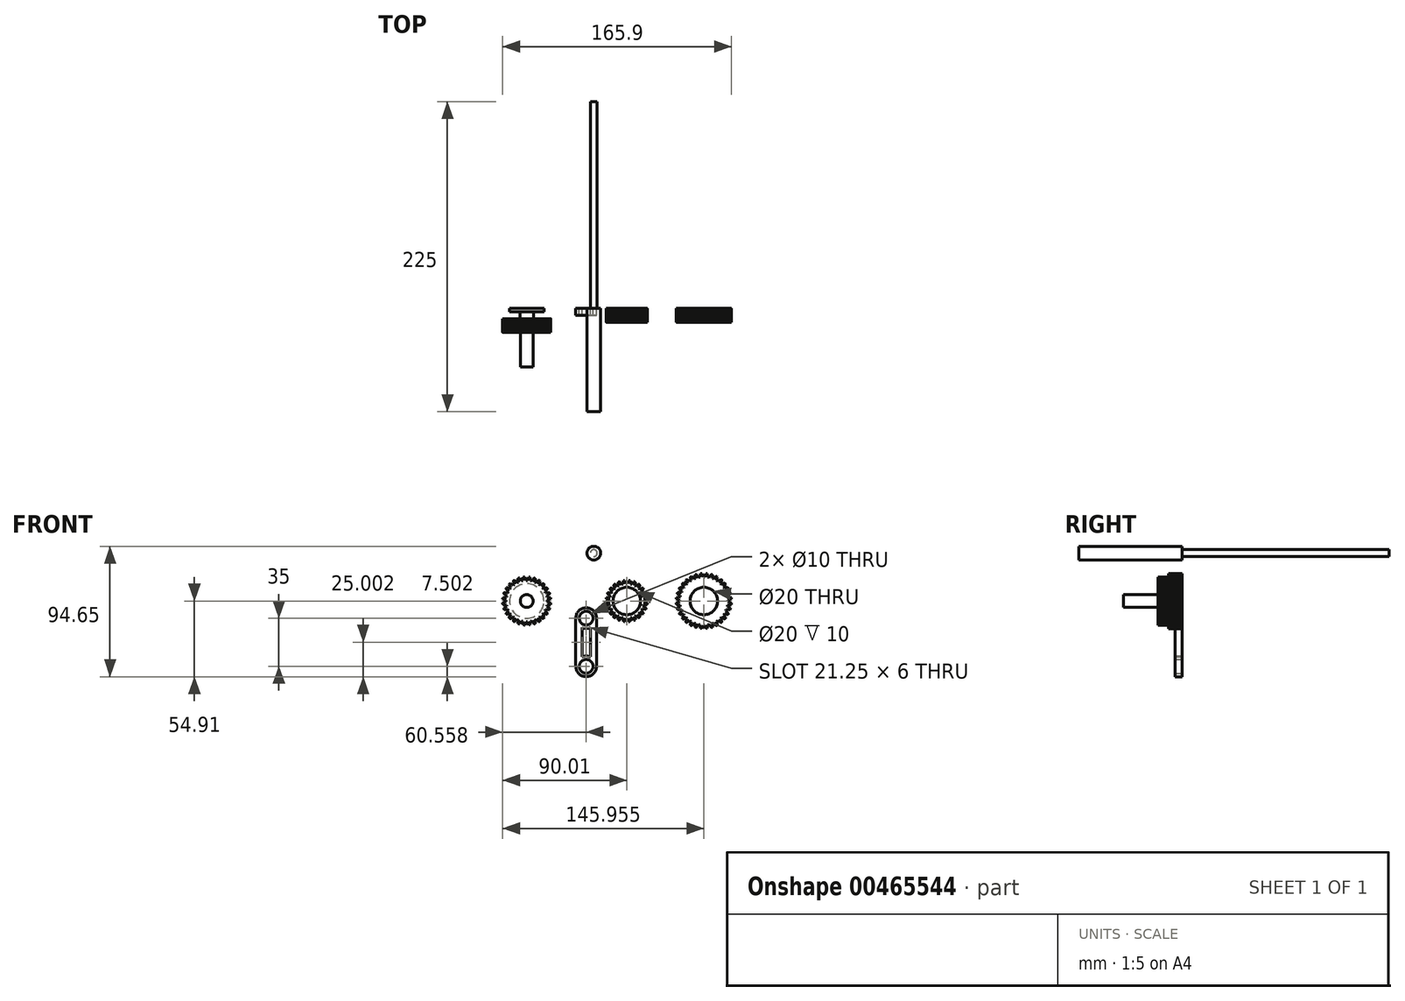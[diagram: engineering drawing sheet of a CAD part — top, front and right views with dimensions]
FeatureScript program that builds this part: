
annotation { "Feature Type Name" : "Feature", "Feature Type Description" : "" }
export const myFeature = defineFeature(function(context is Context, id is Id, definition is map)
    precondition{}
    {
        {
            var Q0;
            Q0=qCreatedBy(makeId("Front.planeOp"),FACE);
            var sketch = newSketch(context, id + "F0", { "sketchPlane" : qUnion([Q0])});
            skCircle(sketch, "E0", {"center": v(0, 0) * mm, "radius": 15 * mm});
            skCircle(sketch, "E1", {"center": v(0, 0) * mm, "radius": 10 * mm});
            skSolve(sketch);
        }
        {
            var Q0;
            Q0=makeQuery(id+"F0.imprint","IMPRINT",FACE,{"disambiguationData":[TD([[makeQuery(id+"F0.imprint","IMPRINT",EDGE,{"derivedFrom":sQuery(id+"F0.wireOp",EDGE,"E0")}),1.0]])]});
            extrude(context, id + "F1", {"entities" : qUnion([Q0]), "depth" : 10 * mm});
        }
        {
            var Q0;
            Q0=makeQuery(id+"F1.opExtrude","CAP_FACE",FACE,{"disambiguationData":[OSD([sQuery(id+"F0.wireOp",EDGE,"E0"),sQuery(id+"F0.wireOp",EDGE,"E1")])],"isStart":false});
            var sketch = newSketch(context, id + "F2", { "sketchPlane" : qUnion([Q0])});
            skLineSegment(sketch, "E2", {"start": v(0, 0) * mm, "end": v(0, 15) * mm, "construction": true});
            skLineSegment(sketch, "E3", {"start": v(0, 12.45) * mm, "end": v(0, 15) * mm, "construction": true});
            skLineSegment(sketch, "E4", {"start": v(0, 12.45) * mm, "end": v(-0.5, 12.45) * mm});
            skLineSegment(sketch, "E5", {"start": v(0, 12.45) * mm, "end": v(0.5, 12.45) * mm});
            skLineSegment(sketch, "E6", {"start": v(-0.5, 12.45) * mm, "end": v(-1.4, 14.93) * mm});
            skLineSegment(sketch, "E7", {"start": v(0.5, 12.45) * mm, "end": v(1.4, 14.93) * mm});
            skSolve(sketch);
        }
        {
            var Q0;
            Q0=makeQuery(id+"F2.imprint","IMPRINT",FACE,{"disambiguationData":[TD([[makeQuery(id+"F2.imprint","IMPRINT",EDGE,{"derivedFrom":sQuery(id+"F2.wireOp",EDGE,"E4")}),-1.0]])]});
            extrude(context, id + "F3", {"entities" : qUnion([Q0]), "operationType" : NewBodyOperationType.REMOVE, "oppositeDirection" : true, "depth" : 25 * mm});
        }
        {
            var Q0;
            Q0=makeQuery(id+"F3.boolean.opBoolean","COPY",FACE,{"derivedFrom":makeQuery(id+"F3.opExtrude","SWEPT_FACE",FACE,{"disambiguationData":[OSD([sQuery(id+"F2.wireOp",EDGE,"E6")])]})});
            var Q1;
            Q1=makeQuery(id+"F3.boolean.opBoolean","COPY",FACE,{"derivedFrom":makeQuery(id+"F3.opExtrude","SWEPT_FACE",FACE,{"disambiguationData":[OSD([sQuery(id+"F2.wireOp",EDGE,"E4"),sQuery(id+"F2.wireOp",EDGE,"E5")])]})});
            var Q2;
            Q2=makeQuery(id+"F3.boolean.opBoolean","COPY",FACE,{"derivedFrom":makeQuery(id+"F3.opExtrude","SWEPT_FACE",FACE,{"disambiguationData":[OSD([sQuery(id+"F2.wireOp",EDGE,"E7")])]})});
            var Q3;
            Q3=makeQuery(id+"F1.opExtrude","SWEPT_FACE",FACE,{"disambiguationData":[OSD([sQuery(id+"F0.wireOp",EDGE,"E0")])]});
            circularPattern(context, id + "F4", {"patternType" : PatternType.FACE, "faces" : qUnion([Q0, Q1, Q2]), "axis" : qUnion([Q3]), "angle" : 360 * degree, "instanceCount" : 24, "equalSpace" : true});
        }
        {
            var Q0;
            Q0=qCreatedBy(makeId("Front.planeOp"),FACE);
            var sketch = newSketch(context, id + "F5", { "sketchPlane" : qUnion([Q0])});
            skCircle(sketch, "E8", {"center": v(-72.57, 0) * mm, "radius": 12.5 * mm});
            skSolve(sketch);
        }
        {
            var Q0;
            Q0=makeQuery(id+"F5.imprint","IMPRINT",FACE,{"disambiguationData":[TD([[makeQuery(id+"F5.imprint","IMPRINT",EDGE,{"derivedFrom":sQuery(id+"F5.wireOp",EDGE,"E8")}),1.0]])]});
            extrude(context, id + "F6", {"entities" : qUnion([Q0]), "depth" : 2.5 * mm});
        }
        {
            var Q0;
            Q0=makeQuery(id+"F6.opExtrude","CAP_FACE",FACE,{"disambiguationData":[OSD([sQuery(id+"F5.wireOp",EDGE,"E8")])],"isStart":false});
            var sketch = newSketch(context, id + "F7", { "sketchPlane" : qUnion([Q0])});
            skLineSegment(sketch, "E9", {"start": v(-72.57, 0) * mm, "end": v(-72.57, 12.5) * mm, "construction": true});
            skLineSegment(sketch, "E10", {"start": v(-72.57, 0) * mm, "end": v(-72.57, -12.5) * mm, "construction": true});
            skCircle(sketch, "E11", {"center": v(-72.57, 0) * mm, "radius": 5 * mm});
            skSolve(sketch);
        }
        {
            var Q0;
            Q0=makeQuery(id+"F7.imprint","IMPRINT",FACE,{"disambiguationData":[TD([[makeQuery(id+"F7.imprint","IMPRINT",EDGE,{"derivedFrom":sQuery(id+"F7.wireOp",EDGE,"E11")}),1.0]])]});
            extrude(context, id + "F8", {"entities" : qUnion([Q0]), "depth" : 5 * mm});
        }
        {
            var Q0;
            Q0=makeQuery(id+"F8.opExtrude","CAP_FACE",FACE,{"disambiguationData":[OSD([sQuery(id+"F7.wireOp",EDGE,"E11")])],"isStart":false});
            var sketch = newSketch(context, id + "F9", { "sketchPlane" : qUnion([Q0])});
            skCircle(sketch, "E12", {"center": v(-72.57, 0) * mm, "radius": 17.5 * mm});
            skSolve(sketch);
        }
        {
            var Q0;
            Q0=makeQuery(id+"F9.imprint","IMPRINT",FACE,{"disambiguationData":[TD([[makeQuery(id+"F9.imprint","IMPRINT",EDGE,{"derivedFrom":sQuery(id+"F9.wireOp",EDGE,"E12")}),1.0]])]});
            var Q1;
            Q1=makeQuery(id+"F9.imprint","IMPRINT",FACE,{"disambiguationData":[TD([[makeQuery(id+"F9.imprint","IMPRINT",EDGE,{"derivedFrom":makeQuery(id+"F8.opExtrude","CAP_EDGE",EDGE,{"disambiguationData":[OSD([sQuery(id+"F7.wireOp",EDGE,"E11")])],"isStart":false})}),1.0]])]});
            extrude(context, id + "F10", {"entities" : qUnion([Q0, Q1]), "operationType" : NewBodyOperationType.ADD, "depth" : 10 * mm});
        }
        {
            var Q0;
            Q0=makeQuery(id+"F10.opExtrude","CAP_FACE",FACE,{"disambiguationData":[OSD([sQuery(id+"F9.wireOp",EDGE,"E12")])],"isStart":false});
            var sketch = newSketch(context, id + "F11", { "sketchPlane" : qUnion([Q0])});
            skLineSegment(sketch, "E13", {"start": v(-72.57, 0) * mm, "end": v(-72.57, 17.5) * mm, "construction": true});
            skLineSegment(sketch, "E14", {"start": v(-72.57, 17.5) * mm, "end": v(-72.57, 14.95) * mm, "construction": true});
            skLineSegment(sketch, "E15", {"start": v(-72.57, 14.95) * mm, "end": v(-72.07, 14.95) * mm});
            skLineSegment(sketch, "E16", {"start": v(-72.57, 14.95) * mm, "end": v(-73.07, 14.95) * mm});
            skLineSegment(sketch, "E17", {"start": v(-73.07, 14.95) * mm, "end": v(-73.98, 17.44) * mm});
            skLineSegment(sketch, "E18", {"start": v(-72.07, 14.95) * mm, "end": v(-71.16, 17.44) * mm});
            skSolve(sketch);
        }
        {
            var Q0;
            Q0=makeQuery(id+"F11.imprint","IMPRINT",FACE,{"disambiguationData":[TD([[makeQuery(id+"F11.imprint","IMPRINT",EDGE,{"derivedFrom":sQuery(id+"F11.wireOp",EDGE,"E15")}),1.0]])]});
            extrude(context, id + "F12", {"entities" : qUnion([Q0]), "operationType" : NewBodyOperationType.REMOVE, "oppositeDirection" : true, "depth" : 25 * mm});
        }
        {
            var Q0;
            Q0=makeQuery(id+"F12.boolean.opBoolean","COPY",FACE,{"derivedFrom":makeQuery(id+"F12.opExtrude","SWEPT_FACE",FACE,{"disambiguationData":[OSD([sQuery(id+"F11.wireOp",EDGE,"E17")])]})});
            var Q1;
            Q1=makeQuery(id+"F12.boolean.opBoolean","COPY",FACE,{"derivedFrom":makeQuery(id+"F12.opExtrude","SWEPT_FACE",FACE,{"disambiguationData":[OSD([sQuery(id+"F11.wireOp",EDGE,"E15"),sQuery(id+"F11.wireOp",EDGE,"E16")])]})});
            var Q2;
            Q2=makeQuery(id+"F12.boolean.opBoolean","COPY",FACE,{"derivedFrom":makeQuery(id+"F12.opExtrude","SWEPT_FACE",FACE,{"disambiguationData":[OSD([sQuery(id+"F11.wireOp",EDGE,"E18")])]})});
            var Q3;
            Q3=makeQuery(id+"F10.opExtrude","SWEPT_FACE",FACE,{"disambiguationData":[OSD([sQuery(id+"F9.wireOp",EDGE,"E12")])]});
            circularPattern(context, id + "F13", {"patternType" : PatternType.FACE, "faces" : qUnion([Q0, Q1, Q2]), "axis" : qUnion([Q3]), "angle" : 360 * degree, "instanceCount" : 28, "equalSpace" : true});
        }
        {
            var Q0;
            Q0=makeQuery(id+"F10.opExtrude","CAP_FACE",FACE,{"disambiguationData":[OSD([sQuery(id+"F9.wireOp",EDGE,"E12")])],"isStart":false});
            var sketch = newSketch(context, id + "F14", { "sketchPlane" : qUnion([Q0])});
            skCircle(sketch, "E19", {"center": v(-72.57, 0) * mm, "radius": 4.64 * mm});
            skSolve(sketch);
        }
        {
            var Q0;
            Q0=makeQuery(id+"F14.imprint","IMPRINT",FACE,{"disambiguationData":[TD([[makeQuery(id+"F14.imprint","IMPRINT",EDGE,{"derivedFrom":sQuery(id+"F14.wireOp",EDGE,"E19")}),1.0]])]});
            extrude(context, id + "F15", {"entities" : qUnion([Q0]), "operationType" : NewBodyOperationType.ADD, "depth" : 25 * mm});
        }
        {
            var Q0;
            Q0=qCreatedBy(makeId("Front.planeOp"),FACE);
            var sketch = newSketch(context, id + "F16", { "sketchPlane" : qUnion([Q0])});
            skCircle(sketch, "E20", {"center": v(55.94, 0) * mm, "radius": 10 * mm});
            skCircle(sketch, "E21", {"center": v(55.94, 0) * mm, "radius": 20 * mm});
            skSolve(sketch);
        }
        {
            var Q0;
            Q0=makeQuery(id+"F16.imprint","IMPRINT",FACE,{"disambiguationData":[TD([[makeQuery(id+"F16.imprint","IMPRINT",EDGE,{"derivedFrom":sQuery(id+"F16.wireOp",EDGE,"E20")}),-1.0]])]});
            extrude(context, id + "F17", {"entities" : qUnion([Q0]), "depth" : 10 * mm});
        }
        {
            var Q0;
            Q0=makeQuery(id+"F17.opExtrude","CAP_FACE",FACE,{"disambiguationData":[OSD([sQuery(id+"F16.wireOp",EDGE,"E20"),sQuery(id+"F16.wireOp",EDGE,"E21")])],"isStart":false});
            var sketch = newSketch(context, id + "F18", { "sketchPlane" : qUnion([Q0])});
            skLineSegment(sketch, "E22", {"start": v(55.94, 0) * mm, "end": v(55.94, 20) * mm, "construction": true});
            skLineSegment(sketch, "E23", {"start": v(55.94, 20) * mm, "end": v(55.94, 17.45) * mm, "construction": true});
            skLineSegment(sketch, "E24", {"start": v(55.94, 17.45) * mm, "end": v(55.44, 17.45) * mm});
            skLineSegment(sketch, "E25", {"start": v(55.94, 17.45) * mm, "end": v(56.44, 17.45) * mm});
            skLineSegment(sketch, "E26", {"start": v(55.44, 17.45) * mm, "end": v(54.53, 19.95) * mm});
            skLineSegment(sketch, "E27", {"start": v(56.44, 17.45) * mm, "end": v(57.35, 19.95) * mm});
            skSolve(sketch);
        }
        {
            var Q0;
            Q0=makeQuery(id+"F18.imprint","IMPRINT",FACE,{"disambiguationData":[TD([[makeQuery(id+"F18.imprint","IMPRINT",EDGE,{"derivedFrom":sQuery(id+"F18.wireOp",EDGE,"E24")}),-1.0]])]});
            extrude(context, id + "F19", {"entities" : qUnion([Q0]), "operationType" : NewBodyOperationType.REMOVE, "oppositeDirection" : true, "depth" : 25 * mm});
        }
        {
            var Q0;
            Q0=makeQuery(id+"F19.boolean.opBoolean","COPY",FACE,{"derivedFrom":makeQuery(id+"F19.opExtrude","SWEPT_FACE",FACE,{"disambiguationData":[OSD([sQuery(id+"F18.wireOp",EDGE,"E26")])]})});
            var Q1;
            Q1=makeQuery(id+"F19.boolean.opBoolean","COPY",FACE,{"derivedFrom":makeQuery(id+"F19.opExtrude","SWEPT_FACE",FACE,{"disambiguationData":[OSD([sQuery(id+"F18.wireOp",EDGE,"E24"),sQuery(id+"F18.wireOp",EDGE,"E25")])]})});
            var Q2;
            Q2=makeQuery(id+"F19.boolean.opBoolean","COPY",FACE,{"derivedFrom":makeQuery(id+"F19.opExtrude","SWEPT_FACE",FACE,{"disambiguationData":[OSD([sQuery(id+"F18.wireOp",EDGE,"E27")])]})});
            var Q3;
            Q3=makeQuery(id+"F17.opExtrude","SWEPT_FACE",FACE,{"disambiguationData":[OSD([sQuery(id+"F16.wireOp",EDGE,"E21")])]});
            circularPattern(context, id + "F20", {"patternType" : PatternType.FACE, "faces" : qUnion([Q0, Q1, Q2]), "axis" : qUnion([Q3]), "angle" : 360 * degree, "instanceCount" : 32, "equalSpace" : true});
        }
        {
            var Q0;
            Q0=qCreatedBy(makeId("Front.planeOp"),FACE);
            var sketch = newSketch(context, id + "F21", { "sketchPlane" : qUnion([Q0])});
            skCircle(sketch, "E28", {"center": v(-23.91, 34.74) * mm, "radius": 5 * mm});
            skSolve(sketch);
        }
        {
            var Q0;
            Q0=makeQuery(id+"F21.imprint","IMPRINT",FACE,{"disambiguationData":[TD([[makeQuery(id+"F21.imprint","IMPRINT",EDGE,{"derivedFrom":sQuery(id+"F21.wireOp",EDGE,"E28")}),1.0]])]});
            extrude(context, id + "F22", {"entities" : qUnion([Q0]), "depth" : 75 * mm});
        }
        {
            var Q0;
            Q0=makeQuery(id+"F22.opExtrude","CAP_FACE",FACE,{"disambiguationData":[OSD([sQuery(id+"F21.wireOp",EDGE,"E28")])],"isStart":true});
            var sketch = newSketch(context, id + "F23", { "sketchPlane" : qUnion([Q0])});
            skCircle(sketch, "E29", {"center": v(23.91, 34.74) * mm, "radius": 2.5 * mm});
            skSolve(sketch);
        }
        {
            var Q0;
            Q0=makeQuery(id+"F23.imprint","IMPRINT",FACE,{"disambiguationData":[TD([[makeQuery(id+"F23.imprint","IMPRINT",EDGE,{"derivedFrom":sQuery(id+"F23.wireOp",EDGE,"E29")}),1.0]])]});
            extrude(context, id + "F24", {"entities" : qUnion([Q0]), "operationType" : NewBodyOperationType.ADD, "depth" : 150 * mm});
        }
        {
            var Q0;
            Q0=qCreatedBy(makeId("Front.planeOp"),FACE);
            var sketch = newSketch(context, id + "F25", { "sketchPlane" : qUnion([Q0])});
            skCircle(sketch, "E30", {"center": v(-29.45, -12.4) * mm, "radius": 5 * mm});
            skLineSegment(sketch, "E31", {"start": v(-29.45, -12.4) * mm, "end": v(-29.45, -47.4) * mm, "construction": true});
            skCircle(sketch, "E32", {"center": v(-29.45, -47.4) * mm, "radius": 5 * mm});
            skCircle(sketch, "E33", {"center": v(-29.45, -12.4) * mm, "radius": 7.5 * mm});
            skCircle(sketch, "E34", {"center": v(-29.45, -47.4) * mm, "radius": 7.5 * mm});
            skLineSegment(sketch, "E35", {"start": v(-36.95, -12.4) * mm, "end": v(-36.95, -47.4) * mm});
            skLineSegment(sketch, "E36", {"start": v(-21.95, -47.4) * mm, "end": v(-21.95, -12.4) * mm});
            skPoint(sketch, "E37", {"position": v(-29.45, -39.9) * mm});
            skPoint(sketch, "E38", {"position": v(-29.45, -19.9) * mm});
            skLineSegment(sketch, "E39", {"start": v(-32.45, -39.9) * mm, "end": v(-32.45, -19.9) * mm});
            skLineSegment(sketch, "E40", {"start": v(-26.45, -19.9) * mm, "end": v(-26.45, -40.53) * mm});
            skLineSegment(sketch, "E41", {"start": v(-32.45, -39.9) * mm, "end": v(-32.45, -40.53) * mm});
            skLineSegment(sketch, "E42", {"start": v(-32.45, -19.9) * mm, "end": v(-32.45, -19.28) * mm});
            skLineSegment(sketch, "E43", {"start": v(-26.45, -19.9) * mm, "end": v(-26.45, -19.28) * mm});
            skSolve(sketch);
        }
        {
            var Q0;
            {var subQ0=sQuery(id+"F25.wireOp",EDGE,"E35");Q0=makeQuery(id+"F25.imprint","IMPRINT",FACE,{"disambiguationData":[TD([[makeQuery(id+"F25.imprint","IMPRINT",EDGE,{"derivedFrom":subQ0}),1.0]])]});}
            var Q1;
            {var subQ1=sQuery(id+"F25.wireOp",EDGE,"E36");Q1=makeQuery(id+"F25.imprint","IMPRINT",FACE,{"disambiguationData":[TD([[makeQuery(id+"F25.imprint","IMPRINT",EDGE,{"derivedFrom":subQ1}),1.0]])]});}
            var Q2;
            Q2=makeQuery(id+"F25.imprint","IMPRINT",FACE,{"disambiguationData":[TD([[makeQuery(id+"F25.imprint","IMPRINT",EDGE,{"derivedFrom":sQuery(id+"F25.wireOp",EDGE,"E32")}),-1.0]])]});
            var Q3;
            Q3=makeQuery(id+"F25.imprint","IMPRINT",FACE,{"disambiguationData":[TD([[makeQuery(id+"F25.imprint","IMPRINT",EDGE,{"derivedFrom":sQuery(id+"F25.wireOp",EDGE,"E30")}),-1.0]])]});
            extrude(context, id + "F26", {"entities" : qUnion([Q0, Q1, Q2, Q3]), "depth" : 5 * mm});
        }
    });
